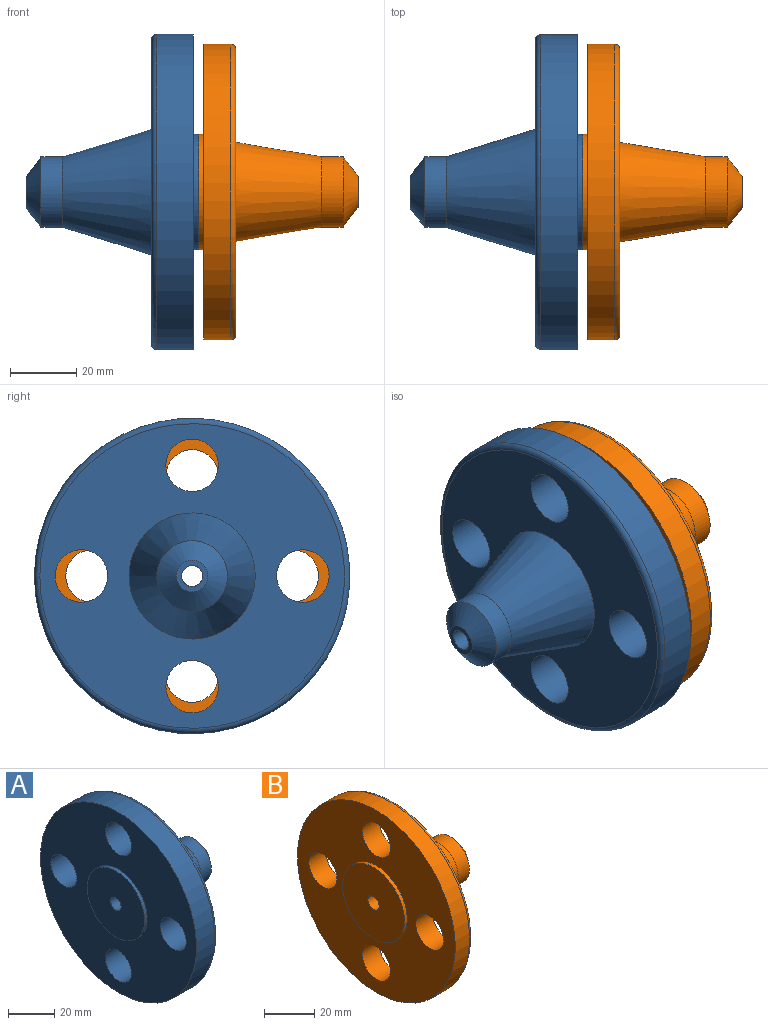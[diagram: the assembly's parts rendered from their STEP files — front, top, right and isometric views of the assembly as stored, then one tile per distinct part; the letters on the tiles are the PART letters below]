
ASSEMBLY  parts=2 mates=1
PART A: 15 faces, bbox 52x102.8x102.8 mm
  f0: cone r=7.71mm half-angle=52.5deg, axis (-1,0,0), area 358.7mm2, adj f1,f13
  f1: cylinder r=10.65mm len=21.3mm, axis (1,0,0), area 428.3mm2, adj f0,f2
  f2: cone r=14.82mm half-angle=17.2deg, axis (-1,0,0), area 2623.3mm2, adj f1,f12
  f3: torus R=45.88mm, axis (1,0,0), area 752.3mm2, adj f4,f12
  f4: cylinder r=47.5mm len=95mm, axis (1,0,0), area 3275.5mm2, adj f3,f11
  f5: cylinder r=17.45mm len=34.9mm, axis (1,0,0), area 175.4mm2, adj f11,f14
  f6: cylinder r=7.9mm len=15.8mm, axis (1,0,0), area 625.4mm2, adj f11,f12
  f7: cylinder r=7.9mm len=15.8mm, axis (1,0,0), area 625.4mm2, adj f11,f12
  f8: cylinder r=7.9mm len=15.8mm, axis (1,0,0), area 625.4mm2, adj f11,f12
  f9: cylinder r=7.9mm len=15.8mm, axis (1,0,0), area 625.4mm2, adj f11,f12
  f10: cylinder r=3.18mm len=52mm, axis (1,0,0), area 1039mm2, adj f13,f14
  f11: plane 95x95mm, normal (-1,0,0), area 5347.3mm2, adj f4,f5,f6,f7,f8,f9
  f12: plane 91.75x91.75mm, normal (1,0,0), area 4693.1mm2, adj f2,f3,f6,f7,f8,f9
  f13: plane 9.56x9.56mm, normal (1,0,0), area 40mm2, adj f0,f10
  f14: plane 34.9x34.9mm, normal (-1,0,0), area 924.9mm2, adj f5,f10
PART B: 15 faces, bbox 48x96.3x96.3 mm
  f0: cone r=7.71mm half-angle=52.5deg, axis (-1,0,0), area 358.7mm2, adj f1,f13
  f1: cylinder r=10.65mm len=21.3mm, axis (1,0,0), area 428.3mm2, adj f0,f2
  f2: cone r=12.82mm half-angle=9.5deg, axis (-1,0,0), area 2116mm2, adj f1,f12
  f3: torus R=43mm, axis (1,0,0), area 650.7mm2, adj f4,f12
  f4: cylinder r=44.5mm len=89mm, axis (1,0,0), area 2264.8mm2, adj f3,f11
  f5: cylinder r=17.45mm len=34.9mm, axis (1,0,0), area 175.4mm2, adj f11,f14
  f6: cylinder r=7.9mm len=15.8mm, axis (1,0,0), area 476.5mm2, adj f11,f12
  f7: cylinder r=7.9mm len=15.8mm, axis (1,0,0), area 476.5mm2, adj f11,f12
  f8: cylinder r=7.9mm len=15.8mm, axis (1,0,0), area 476.5mm2, adj f11,f12
  f9: cylinder r=7.9mm len=15.8mm, axis (1,0,0), area 476.5mm2, adj f11,f12
  f10: cylinder r=3.18mm len=48mm, axis (1,0,0), area 959.1mm2, adj f13,f14
  f11: plane 89x89mm, normal (-1,0,0), area 4480.2mm2, adj f4,f5,f6,f7,f8,f9
  f12: plane 86x86mm, normal (1,0,0), area 4317.7mm2, adj f2,f3,f6,f7,f8,f9
  f13: plane 9.56x9.56mm, normal (1,0,0), area 40mm2, adj f0,f10
  f14: plane 34.9x34.9mm, normal (-1,0,0), area 924.9mm2, adj f5,f10
PLACE A rot(axis=(0,1,0),180deg) t=(-58.79,-7,19.63)mm
PLACE B t=(-58.79,-7,19.63)mm
MATE revolute A.f0 <-> B.f0  axis (1,0,0) through (-58.79,-7,19.63)mm
